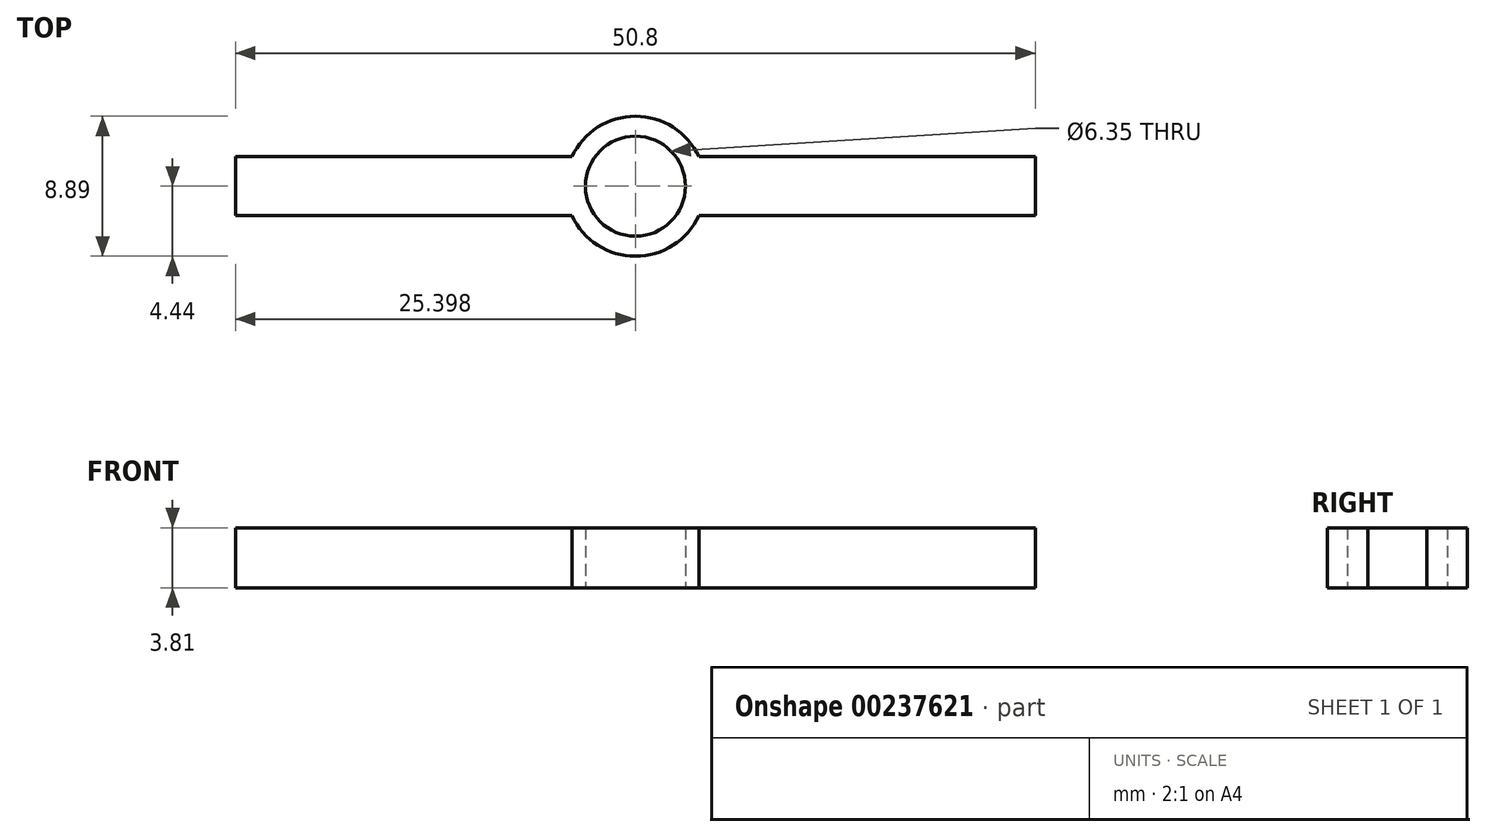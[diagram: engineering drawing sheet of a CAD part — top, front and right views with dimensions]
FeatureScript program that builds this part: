
annotation { "Feature Type Name" : "Feature", "Feature Type Description" : "" }
export const myFeature = defineFeature(function(context is Context, id is Id, definition is map)
    precondition{}
    {
        {
            var Q0;
            Q0=qCreatedBy(makeId("Top.planeOp"),FACE);
            var sketch = newSketch(context, id + "F0", { "sketchPlane" : qUnion([Q0])});
            skLineSegment(sketch, "E0.bottom", {"start": v(2.59, 36.39) * mm, "end": v(-18.78, 36.39) * mm});
            skLineSegment(sketch, "E0.top", {"start": v(2.59, 40.13) * mm, "end": v(-18.78, 40.13) * mm});
            skLineSegment(sketch, "E0.left", {"start": v(2.59, 36.39) * mm, "end": v(2.59, 40.13) * mm});
            skLineSegment(sketch, "E0.right", {"start": v(-48.21, 36.39) * mm, "end": v(-48.21, 40.13) * mm});
            skPoint(sketch, "E0.middle", {"position": v(-22.81, 38.26) * mm});
            skArc(sketch, "E1", {"start": v(-26.84, 36.39) * mm, "mid": v(-22.81, 33.82) * mm, "end": v(-18.78, 36.39) * mm});
            skCircle(sketch, "E2", {"center": v(-22.81, 38.26) * mm, "radius": 3.18 * mm});
            skLineSegment(sketch, "E3.trimOffspring", {"start": v(-26.84, 40.13) * mm, "end": v(-48.21, 40.13) * mm});
            skLineSegment(sketch, "E4.trimOffspring", {"start": v(-26.84, 36.39) * mm, "end": v(-48.21, 36.39) * mm});
            skArc(sketch, "E5.trimOffspring", {"start": v(-18.78, 40.13) * mm, "mid": v(-22.81, 42.7) * mm, "end": v(-26.84, 40.13) * mm});
            skSolve(sketch);
        }
        {
            var Q0;
            Q0 = qSketchRegion(id + "F0", true);
            extrude(context, id + "F1", {"entities" : qUnion([Q0]), "depth" : 3.8 * mm});
        }
    });
